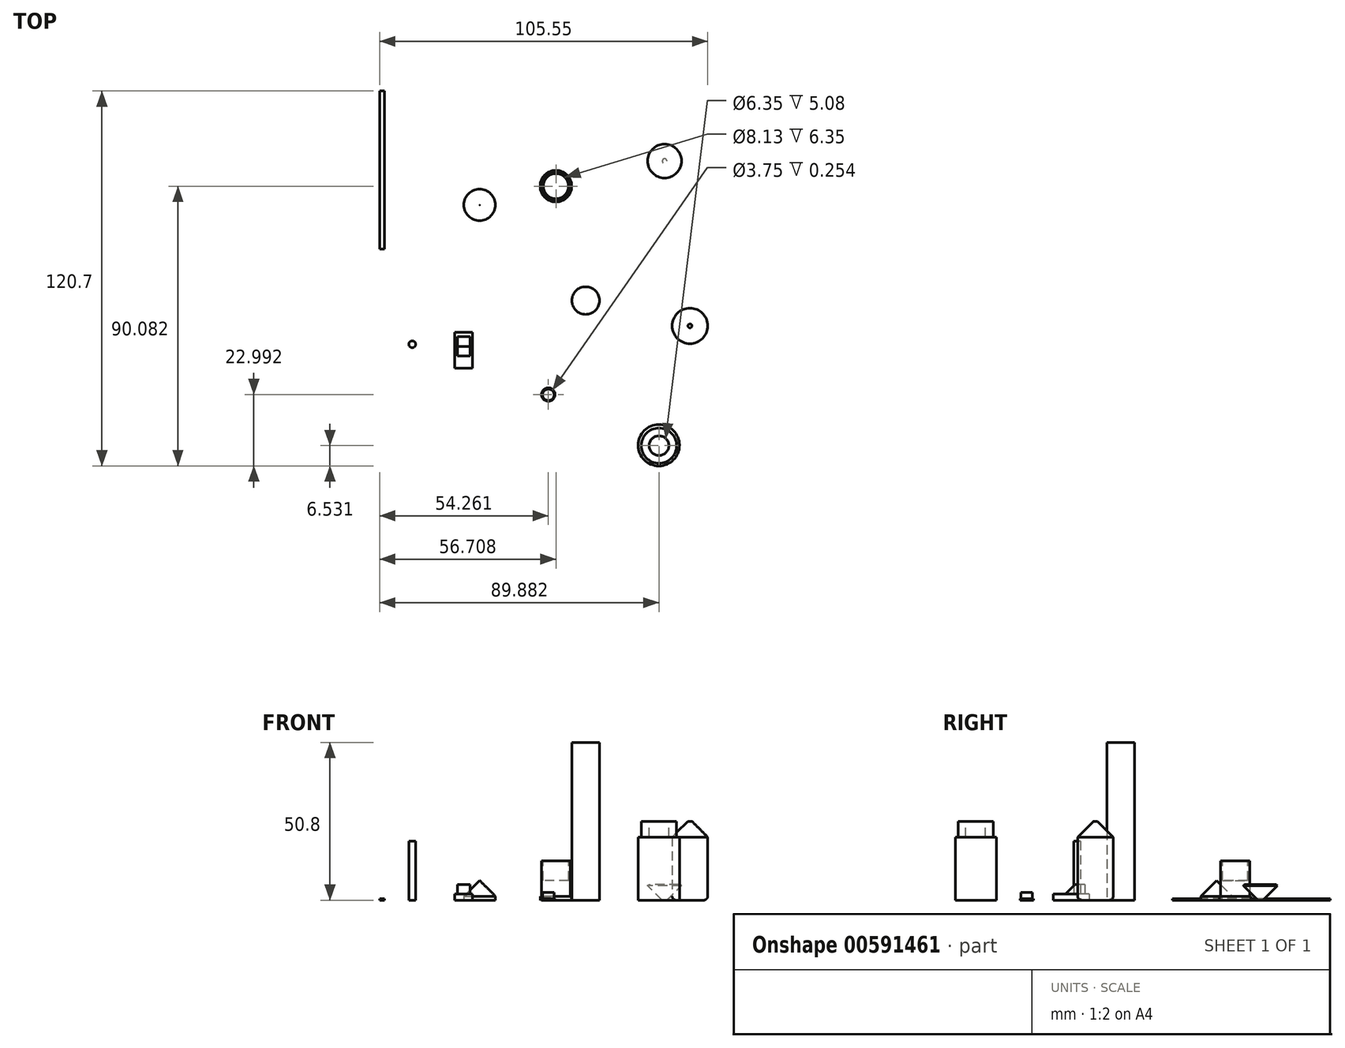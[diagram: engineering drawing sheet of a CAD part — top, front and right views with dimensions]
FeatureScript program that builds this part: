
annotation { "Feature Type Name" : "Feature", "Feature Type Description" : "" }
export const myFeature = defineFeature(function(context is Context, id is Id, definition is map)
    precondition{}
    {
        {
            var Q0;
            Q0=qCreatedBy(makeId("Top.planeOp"),FACE);
            var sketch = newSketch(context, id + "F0", { "sketchPlane" : qUnion([Q0])});
            skCircle(sketch, "E0", {"center": v(0, 0) * mm, "radius": 4.45 * mm});
            skSolve(sketch);
        }
        {
            var Q0;
            Q0 = qSketchRegion(id + "F0", true);
            extrude(context, id + "F1", {"entities" : qUnion([Q0]), "depth" : 50.8 * mm, "offsetDistance" : 25.4 * mm});
        }
        {
            var Q0;
            Q0=qCreatedBy(makeId("Top.planeOp"),FACE);
            var sketch = newSketch(context, id + "F2", { "sketchPlane" : qUnion([Q0])});
            skCircle(sketch, "E1", {"center": v(25.4, 44.92) * mm, "radius": 5.82 * mm});
            skSolve(sketch);
        }
        {
            var Q0;
            Q0 = qSketchRegion(id + "F2", true);
            extrude(context, id + "F3", {"entities" : qUnion([Q0]), "depth" : 5.08 * mm, "offsetDistance" : 25.4 * mm});
        }
        {
            var Q0;
            Q0=makeQuery(id+"F3.opExtrude","CAP_EDGE",EDGE,{"disambiguationData":[OSD([sQuery(id+"F2.wireOp",EDGE,"E1")])],"isStart":false});
            fillet(context, id + "F4", {"entities" : qUnion([Q0]), "radius" : 1.27 * mm, "tangentPropagation" : true, "allowEdgeOverflow" : false});
        }
        {
            var Q0;
            Q0=qCreatedBy(makeId("Top.planeOp"),FACE);
            var sketch = newSketch(context, id + "F5", { "sketchPlane" : qUnion([Q0])});
            skCircle(sketch, "E2", {"center": v(33.56, -8.16) * mm, "radius": 5.72 * mm});
            skSolve(sketch);
        }
        {
            var Q0;
            Q0 = qSketchRegion(id + "F5", true);
            extrude(context, id + "F6", {"entities" : qUnion([Q0]), "depth" : 25.4 * mm, "offsetDistance" : 25.4 * mm});
        }
        {
            var Q0;
            Q0=makeQuery(id+"F6.opExtrude","CAP_FACE",FACE,{"disambiguationData":[OSD([sQuery(id+"F5.wireOp",EDGE,"E2")])],"isStart":true});
            fillet(context, id + "F7", {"entities" : qUnion([Q0]), "radius" : 1.27 * mm, "tangentPropagation" : true, "allowEdgeOverflow" : false});
        }
        {
            var Q0;
            {var subQ0=sQuery(id+"F5.wireOp",EDGE,"E2");Q0=makeQuery(id+"F7.opFillet","BLEND_EDGE",EDGE,{"blendedFrom":[makeQuery(id+"F6.opExtrude","CAP_EDGE",EDGE,{"disambiguationData":[OSD([subQ0])],"isStart":true}),makeQuery(id+"F6.opExtrude","CAP_FACE",FACE,{"disambiguationData":[OSD([subQ0])],"isStart":true})],"blendedInto":[makeQuery(id+"F6.opExtrude","CAP_FACE",FACE,{"disambiguationData":[OSD([subQ0])],"isStart":true})]});}
            var Q1;
            Q1=makeQuery(id+"F6.opExtrude","SWEPT_FACE",FACE,{"disambiguationData":[OSD([sQuery(id+"F5.wireOp",EDGE,"E2")])]});
            chamfer(context, id + "F8", {"entities" : qUnion([Q0, Q1]), "width" : 5.08 * mm, "tangentPropagation" : true});
        }
        {
            var Q0;
            {var subQ0=sQuery(id+"F2.wireOp",EDGE,"E1");Q0=makeQuery(id+"F4.opFillet","BLEND_EDGE",EDGE,{"blendedFrom":[makeQuery(id+"F3.opExtrude","CAP_EDGE",EDGE,{"disambiguationData":[OSD([subQ0])],"isStart":false}),makeQuery(id+"F3.opExtrude","SWEPT_FACE",FACE,{"disambiguationData":[OSD([subQ0])]})],"blendedInto":[makeQuery(id+"F3.opExtrude","SWEPT_FACE",FACE,{"disambiguationData":[OSD([subQ0])]})]});}
            var Q1;
            {var subQ0=sQuery(id+"F2.wireOp",EDGE,"E1");Q1=makeQuery(id+"F4.opFillet","BLEND_EDGE",EDGE,{"blendedFrom":[makeQuery(id+"F3.opExtrude","CAP_EDGE",EDGE,{"disambiguationData":[OSD([subQ0])],"isStart":false}),makeQuery(id+"F3.opExtrude","CAP_FACE",FACE,{"disambiguationData":[OSD([subQ0])],"isStart":false})],"blendedInto":[makeQuery(id+"F3.opExtrude","CAP_FACE",FACE,{"disambiguationData":[OSD([subQ0])],"isStart":false})]});}
            var Q2;
            Q2=makeQuery(id+"F3.opExtrude","CAP_FACE",FACE,{"disambiguationData":[OSD([sQuery(id+"F2.wireOp",EDGE,"E1")])],"isStart":true});
            chamfer(context, id + "F9", {"entities" : qUnion([Q0, Q1, Q2]), "width" : 5.08 * mm, "tangentPropagation" : true});
        }
        {
            var Q0;
            Q0=qCreatedBy(makeId("Top.planeOp"),FACE);
            var sketch = newSketch(context, id + "F10", { "sketchPlane" : qUnion([Q0])});
            skCircle(sketch, "E3", {"center": v(-9.57, 36.83) * mm, "radius": 4.7 * mm});
            skSolve(sketch);
        }
        {
            var Q0;
            Q0 = qSketchRegion(id + "F10", true);
            extrude(context, id + "F11", {"entities" : qUnion([Q0]), "depth" : 12.7 * mm, "offsetDistance" : 25.4 * mm});
        }
        {
            var Q0;
            Q0=makeQuery(id+"F11.opExtrude","CAP_FACE",FACE,{"disambiguationData":[OSD([sQuery(id+"F10.wireOp",EDGE,"E3")])],"isStart":false});
            var sketch = newSketch(context, id + "F12", { "sketchPlane" : qUnion([Q0])});
            skCircle(sketch, "E4", {"center": v(-9.57, 36.83) * mm, "radius": 4.06 * mm});
            skSolve(sketch);
        }
        {
            var Q0;
            Q0=makeQuery(id+"F12.imprint","IMPRINT",FACE,{"disambiguationData":[TD([[makeQuery(id+"F12.imprint","IMPRINT",EDGE,{"derivedFrom":sQuery(id+"F12.wireOp",EDGE,"E4")}),1.0]])]});
            extrude(context, id + "F13", {"entities" : qUnion([Q0]), "operationType" : NewBodyOperationType.REMOVE, "oppositeDirection" : true, "depth" : 6.35 * mm, "offsetDistance" : 25.4 * mm});
        }
        {
            var Q0;
            Q0=makeQuery(id+"F11.opExtrude","CAP_FACE",FACE,{"disambiguationData":[OSD([sQuery(id+"F10.wireOp",EDGE,"E3")])],"isStart":true});
            var sketch = newSketch(context, id + "F14", { "sketchPlane" : qUnion([Q0])});
            skCircle(sketch, "E5", {"center": v(-9.57, -36.83) * mm, "radius": 5.07 * mm});
            skSolve(sketch);
        }
        {
            var Q0;
            Q0 = qSketchRegion(id + "F14", true);
            extrude(context, id + "F15", {"entities" : qUnion([Q0]), "operationType" : NewBodyOperationType.ADD, "oppositeDirection" : true, "depth" : 1.27 * mm, "offsetDistance" : 25.4 * mm});
        }
        {
            var Q0;
            Q0=qCreatedBy(makeId("Top.planeOp"),FACE);
            var sketch = newSketch(context, id + "F16", { "sketchPlane" : qUnion([Q0])});
            skCircle(sketch, "E6", {"center": v(-34.12, 30.8) * mm, "radius": 5.08 * mm});
            skSolve(sketch);
        }
        {
            var Q0;
            Q0 = qSketchRegion(id + "F16", true);
            extrude(context, id + "F17", {"entities" : qUnion([Q0]), "depth" : 6.35 * mm, "offsetDistance" : 25.4 * mm});
        }
        {
            var Q0;
            Q0=makeQuery(id+"F17.opExtrude","CAP_FACE",FACE,{"disambiguationData":[OSD([sQuery(id+"F16.wireOp",EDGE,"E6")])],"isStart":false});
            chamfer(context, id + "F18", {"entities" : qUnion([Q0]), "width" : 5.08 * mm, "tangentPropagation" : true});
        }
        {
            var Q0;
            Q0=qCreatedBy(makeId("Top.planeOp"),FACE);
            var sketch = newSketch(context, id + "F19", { "sketchPlane" : qUnion([Q0])});
            skCircle(sketch, "E7", {"center": v(-55.8, -14.07) * mm, "radius": 1.1 * mm});
            skSolve(sketch);
        }
        {
            var Q0;
            Q0 = qSketchRegion(id + "F19", true);
            extrude(context, id + "F20", {"entities" : qUnion([Q0]), "depth" : 19.05 * mm, "offsetDistance" : 25.4 * mm});
        }
        {
            var Q0;
            Q0=qCreatedBy(makeId("Top.planeOp"),FACE);
            var sketch = newSketch(context, id + "F21", { "sketchPlane" : qUnion([Q0])});
            skLineSegment(sketch, "E8.bottom", {"start": v(-41.32, -11.56) * mm, "end": v(-37.17, -11.56) * mm});
            skLineSegment(sketch, "E8.top", {"start": v(-41.32, -19.86) * mm, "end": v(-37.17, -19.86) * mm});
            skLineSegment(sketch, "E8.left", {"start": v(-41.32, -11.56) * mm, "end": v(-41.32, -19.86) * mm});
            skLineSegment(sketch, "E8.right", {"start": v(-37.17, -11.56) * mm, "end": v(-37.17, -19.86) * mm});
            skSolve(sketch);
        }
        {
            var Q0;
            Q0 = qSketchRegion(id + "F21", true);
            extrude(context, id + "F22", {"entities" : qUnion([Q0]), "depth" : 5.08 * mm, "offsetDistance" : 25.4 * mm});
        }
        {
            var Q0;
            Q0=makeQuery(id+"F22.opExtrude","CAP_EDGE",EDGE,{"disambiguationData":[OSD([sQuery(id+"F21.wireOp",EDGE,"E8.top")])],"isStart":false});
            chamfer(context, id + "F23", {"entities" : qUnion([Q0]), "width" : 5.08 * mm, "tangentPropagation" : true});
        }
        {
            var Q0;
            Q0=qCreatedBy(makeId("Top.planeOp"),FACE);
            var sketch = newSketch(context, id + "F24", { "sketchPlane" : qUnion([Q0])});
            skLineSegment(sketch, "E9.bottom", {"start": v(-42.1, -10.22) * mm, "end": v(-36.4, -10.22) * mm});
            skLineSegment(sketch, "E9.top", {"start": v(-42.1, -21.77) * mm, "end": v(-36.4, -21.77) * mm});
            skLineSegment(sketch, "E9.left", {"start": v(-42.1, -10.22) * mm, "end": v(-42.1, -21.77) * mm});
            skLineSegment(sketch, "E9.right", {"start": v(-36.4, -10.22) * mm, "end": v(-36.4, -21.77) * mm});
            skSolve(sketch);
        }
        {
            var Q0;
            Q0 = qSketchRegion(id + "F24", true);
            extrude(context, id + "F25", {"entities" : qUnion([Q0]), "operationType" : NewBodyOperationType.ADD, "depth" : 2.03 * mm, "offsetDistance" : 25.4 * mm});
        }
        {
            var Q0;
            Q0=qCreatedBy(makeId("Top.planeOp"),FACE);
            var sketch = newSketch(context, id + "F26", { "sketchPlane" : qUnion([Q0])});
            skLineSegment(sketch, "E10.bottom", {"start": v(-66.28, 67.45) * mm, "end": v(-64.71, 67.45) * mm});
            skLineSegment(sketch, "E10.top", {"start": v(-66.28, 16.6) * mm, "end": v(-64.71, 16.6) * mm});
            skLineSegment(sketch, "E10.left", {"start": v(-66.28, 67.45) * mm, "end": v(-66.28, 16.6) * mm});
            skLineSegment(sketch, "E10.right", {"start": v(-64.71, 67.45) * mm, "end": v(-64.71, 16.6) * mm});
            skSolve(sketch);
        }
        {
            var Q0;
            Q0 = qSketchRegion(id + "F26", true);
            extrude(context, id + "F27", {"entities" : qUnion([Q0]), "depth" : 0.5 * mm, "offsetDistance" : 25.4 * mm});
        }
        {
            var Q0;
            Q0=qCreatedBy(makeId("Top.planeOp"),FACE);
            var sketch = newSketch(context, id + "F28", { "sketchPlane" : qUnion([Q0])});
            skCircle(sketch, "E11", {"center": v(23.6, -46.72) * mm, "radius": 5.68 * mm});
            skSolve(sketch);
        }
        {
            var Q0;
            Q0 = qSketchRegion(id + "F28", true);
            extrude(context, id + "F29", {"entities" : qUnion([Q0]), "depth" : 25.4 * mm, "offsetDistance" : 25.4 * mm});
        }
        {
            var Q0;
            Q0=makeQuery(id+"F29.opExtrude","CAP_FACE",FACE,{"disambiguationData":[OSD([sQuery(id+"F28.wireOp",EDGE,"E11")])],"isStart":false});
            var sketch = newSketch(context, id + "F30", { "sketchPlane" : qUnion([Q0])});
            skPoint(sketch, "E12", {"position": v(23.6, -46.72) * mm});
            skSolve(sketch);
        }
        {
            var Q0;
            Q0=sQuery(id+"F30.wireOp",VERTEX,"E12");
            var Q1;
            Q1=makeQuery(id+"F29.opExtrude","SWEPT_BODY",BODY,{"disambiguationData":[OSD([sQuery(id+"F28.wireOp",EDGE,"E11")])]});
            hole(context, id + "F31", {"style" : HoleStyle.SIMPLE, "endStyle" : HoleEndStyle.THROUGH, "holeDiameter" : 6.35 * mm, "majorDiameter" : 6.35 * mm, "isTappedThrough" : true, "tappedDepth" : 12.7 * mm, "tapClearance" : 3, "locations" : qUnion([Q0]), "scope" : qUnion([Q1])});
        }
        {
            var Q0;
            Q0=qCreatedBy(makeId("Top.planeOp"),FACE);
            var sketch = newSketch(context, id + "F32", { "sketchPlane" : qUnion([Q0])});
            skCircle(sketch, "E13", {"center": v(23.55, -46.6) * mm, "radius": 6.65 * mm});
            skSolve(sketch);
        }
        {
            var Q0;
            Q0 = qSketchRegion(id + "F32", true);
            extrude(context, id + "F33", {"entities" : qUnion([Q0]), "operationType" : NewBodyOperationType.ADD, "depth" : 20.32 * mm, "offsetDistance" : 25.4 * mm});
        }
        {
            var Q0;
            Q0=qCreatedBy(makeId("Top.planeOp"),FACE);
            var sketch = newSketch(context, id + "F34", { "sketchPlane" : qUnion([Q0])});
            skCircle(sketch, "E14", {"center": v(-11.99, -30.35) * mm, "radius": 1.85 * mm});
            skSolve(sketch);
        }
        {
            var Q0;
            Q0 = qSketchRegion(id + "F34", true);
            extrude(context, id + "F35", {"entities" : qUnion([Q0]), "depth" : 2.54 * mm, "offsetDistance" : 25.4 * mm});
        }
        {
            var Q0;
            Q0=qCreatedBy(makeId("Top.planeOp"),FACE);
            var sketch = newSketch(context, id + "F36", { "sketchPlane" : qUnion([Q0])});
            skCircle(sketch, "E15", {"center": v(-12.02, -30.26) * mm, "radius": 2.17 * mm});
            skSolve(sketch);
        }
        {
            var Q0;
            Q0 = qSketchRegion(id + "F36", true);
            extrude(context, id + "F37", {"entities" : qUnion([Q0]), "operationType" : NewBodyOperationType.ADD, "depth" : 0.5 * mm, "offsetDistance" : 25.4 * mm});
        }
        {
            var Q0;
            Q0=makeQuery(id+"F37.boolean.opBoolean","MERGE",FACE,{"derivedFrom":[makeQuery(id+"F35.opExtrude","CAP_FACE",FACE,{"disambiguationData":[OSD([sQuery(id+"F34.wireOp",EDGE,"E14")])],"isStart":true}),makeQuery(id+"F37.opExtrude","CAP_FACE",FACE,{"disambiguationData":[OSD([sQuery(id+"F36.wireOp",EDGE,"E15")])],"isStart":true})]});
            var sketch = newSketch(context, id + "F38", { "sketchPlane" : qUnion([Q0])});
            skCircle(sketch, "E16", {"center": v(-12.02, 30.26) * mm, "radius": 1.88 * mm});
            skSolve(sketch);
        }
        {
            var Q0;
            Q0 = qSketchRegion(id + "F38", true);
            extrude(context, id + "F39", {"entities" : qUnion([Q0]), "operationType" : NewBodyOperationType.REMOVE, "oppositeDirection" : true, "depth" : 0.25 * mm, "offsetDistance" : 25.4 * mm});
        }
    });
